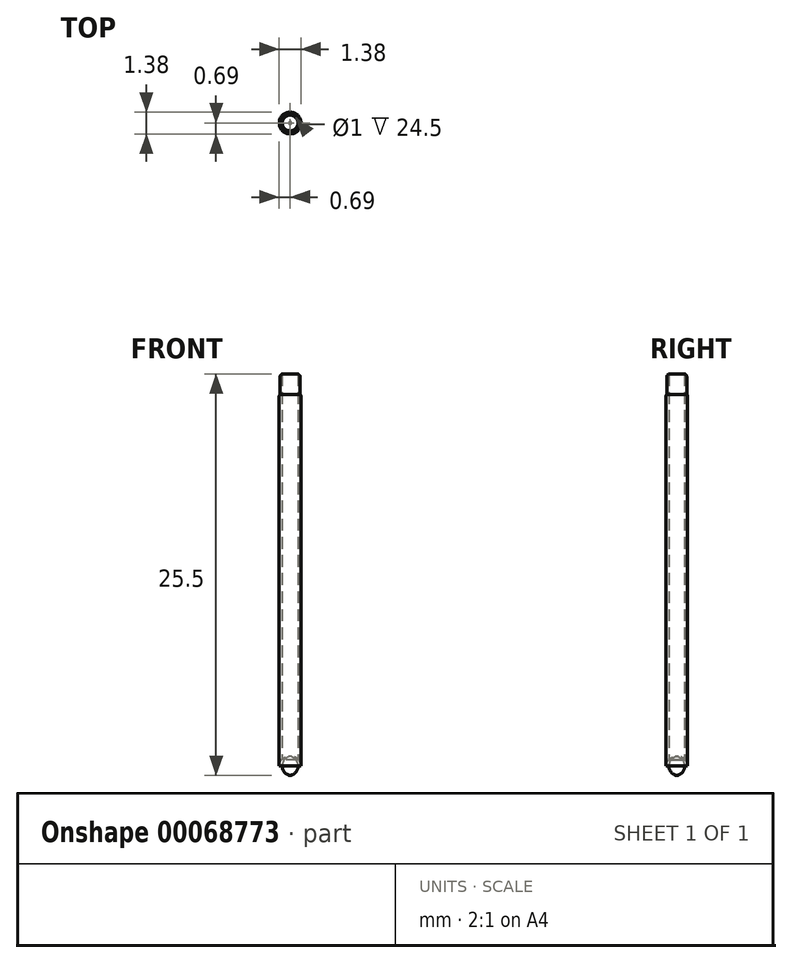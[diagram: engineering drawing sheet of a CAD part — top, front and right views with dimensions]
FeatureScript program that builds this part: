
annotation { "Feature Type Name" : "Feature", "Feature Type Description" : "" }
export const myFeature = defineFeature(function(context is Context, id is Id, definition is map)
    precondition{}
    {
        {
            var Q0;
            Q0=qCreatedBy(makeId("Top.planeOp"),FACE);
            var sketch = newSketch(context, id + "F0", { "sketchPlane" : qUnion([Q0])});
            skCircle(sketch, "E0", {"center": v(0, 0) * mm, "radius": 0.69 * mm});
            skCircle(sketch, "E1", {"center": v(0, 0) * mm, "radius": 0.64 * mm});
            skCircle(sketch, "E2", {"center": v(0, 0) * mm, "radius": 0.5 * mm});
            skSolve(sketch);
        }
        {
            var Q0;
            Q0=makeQuery(id+"F0.imprint","IMPRINT",FACE,{"disambiguationData":[TD([[makeQuery(id+"F0.imprint","IMPRINT",EDGE,{"derivedFrom":sQuery(id+"F0.wireOp",EDGE,"E0")}),1.0]])]});
            extrude(context, id + "F1", {"entities" : qUnion([Q0]), "depth" : 24.2 * mm});
        }
        {
            var Q0;
            Q0=makeQuery(id+"F0.imprint","IMPRINT",FACE,{"disambiguationData":[TD([[makeQuery(id+"F0.imprint","IMPRINT",EDGE,{"derivedFrom":sQuery(id+"F0.wireOp",EDGE,"E1")}),1.0]])]});
            extrude(context, id + "F2", {"entities" : qUnion([Q0]), "operationType" : NewBodyOperationType.ADD, "depth" : 25.5 * mm});
        }
        {
            var Q0;
            Q0=makeQuery(id+"F0.imprint","IMPRINT",FACE,{"disambiguationData":[TD([[makeQuery(id+"F0.imprint","IMPRINT",EDGE,{"derivedFrom":sQuery(id+"F0.wireOp",EDGE,"E2")}),1.0]])]});
            var Q1;
            Q1=makeQuery(id+"F0.imprint","IMPRINT",FACE,{"disambiguationData":[TD([[makeQuery(id+"F0.imprint","IMPRINT",EDGE,{"derivedFrom":sQuery(id+"F0.wireOp",EDGE,"E1")}),1.0]])]});
            var Q2;
            Q2=makeQuery(id+"F0.imprint","IMPRINT",FACE,{"disambiguationData":[TD([[makeQuery(id+"F0.imprint","IMPRINT",EDGE,{"derivedFrom":sQuery(id+"F0.wireOp",EDGE,"E0")}),1.0]])]});
            extrude(context, id + "F3", {"entities" : qUnion([Q0, Q1, Q2]), "operationType" : NewBodyOperationType.ADD, "depth" : 1 * mm});
        }
        {
            var Q0;
            {var subQ0=sQuery(id+"F0.wireOp",EDGE,"E0");Q0=makeQuery(id+"F3.boolean.opBoolean","MERGE",FACE,{"derivedFrom":[makeQuery(id+"F1.opExtrude","CAP_FACE",FACE,{"disambiguationData":[OSD([subQ0,sQuery(id+"F0.wireOp",EDGE,"E1")])],"isStart":true}),makeQuery(id+"F3.opExtrude","CAP_FACE",FACE,{"disambiguationData":[OSD([subQ0])],"isStart":true})]});}
            fillet(context, id + "F4", {"entities" : qUnion([Q0]), "radius" : 0.6 * mm, "tangentPropagation" : true, "allowEdgeOverflow" : false});
        }
        {
            var Q0;
            Q0=makeQuery(id+"F1.opExtrude","CAP_EDGE",EDGE,{"disambiguationData":[OSD([sQuery(id+"F0.wireOp",EDGE,"E0")])],"isStart":false});
            var Q1;
            Q1=makeQuery(id+"F2.opExtrude","CAP_EDGE",EDGE,{"disambiguationData":[OSD([sQuery(id+"F0.wireOp",EDGE,"E1")])],"isStart":false});
            fillet(context, id + "F5", {"entities" : qUnion([Q0, Q1]), "radius" : 0.2 * mm, "tangentPropagation" : true, "allowEdgeOverflow" : false});
        }
        {
            var Q0;
            Q0=qCreatedBy(makeId("Front.planeOp"),FACE);
            var sketch = newSketch(context, id + "F6", { "sketchPlane" : qUnion([Q0])});
            skLineSegment(sketch, "E3.0", {"start": v(-0.5, 25.5) * mm, "end": v(0.5, 25.5) * mm, "construction": true});
            skLineSegment(sketch, "E4", {"start": v(0, 0) * mm, "end": v(0, 18) * mm, "construction": true});
            skSolve(sketch);
        }
    });
